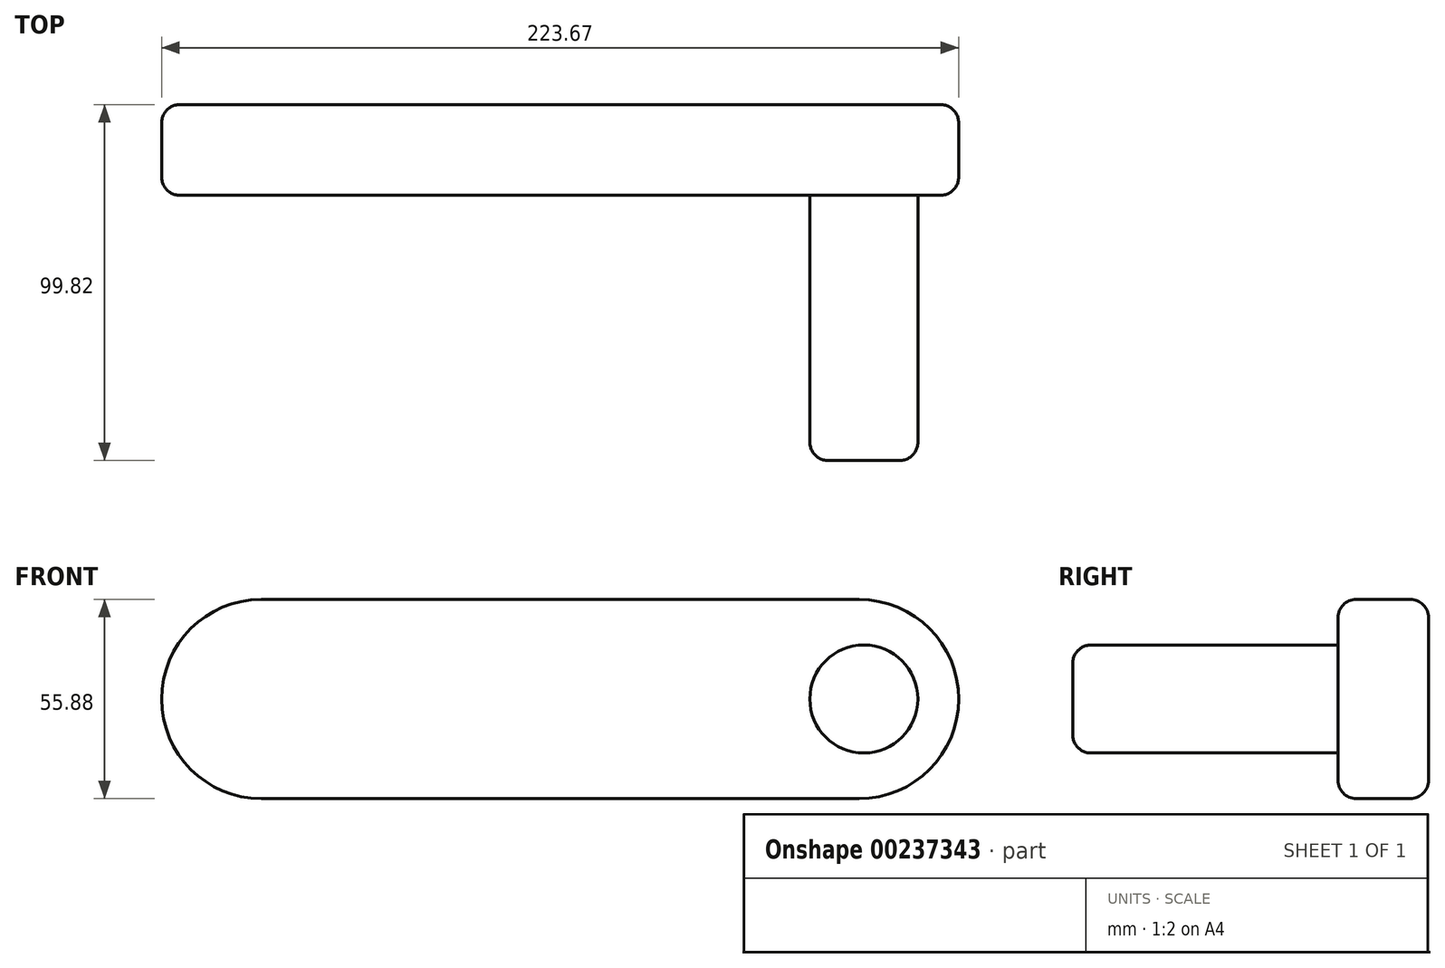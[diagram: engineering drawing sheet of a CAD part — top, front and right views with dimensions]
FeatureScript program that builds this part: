
annotation { "Feature Type Name" : "Feature", "Feature Type Description" : "" }
export const myFeature = defineFeature(function(context is Context, id is Id, definition is map)
    precondition{}
    {
        {
            var Q0;
            Q0=qCreatedBy(makeId("Front.planeOp"),FACE);
            var sketch = newSketch(context, id + "F0", { "sketchPlane" : qUnion([Q0])});
            skCircle(sketch, "E0", {"center": v(-106.88, 0) * mm, "radius": 27.94 * mm});
            skCircle(sketch, "E1", {"center": v(60.9, 0) * mm, "radius": 27.94 * mm});
            skLineSegment(sketch, "E2", {"start": v(-106.88, 27.94) * mm, "end": v(60.9, 27.94) * mm});
            skLineSegment(sketch, "E3", {"start": v(-106.88, -27.94) * mm, "end": v(60.9, -27.94) * mm});
            skSolve(sketch);
        }
        {
            var Q0;
            Q0 = qSketchRegion(id + "F0", true);
            extrude(context, id + "F1", {"entities" : qUnion([Q0]), "depth" : 25.4 * mm});
        }
        {
            var Q0;
            Q0=qCreatedBy(makeId("Front.planeOp"),FACE);
            var sketch = newSketch(context, id + "F2", { "sketchPlane" : qUnion([Q0])});
            skCircle(sketch, "E4", {"center": v(62.24, 0) * mm, "radius": 15.15 * mm});
            skSolve(sketch);
        }
        {
            var Q0;
            Q0 = qSketchRegion(id + "F2", true);
            extrude(context, id + "F3", {"entities" : qUnion([Q0]), "operationType" : NewBodyOperationType.ADD, "depth" : 71.37 * mm});
        }
        {
            var Q0;
            Q0=makeQuery(id+"F3.opExtrude","CAP_FACE",FACE,{"disambiguationData":[OSD([sQuery(id+"F2.wireOp",EDGE,"E4")])],"isStart":false});
            extrude(context, id + "F4", {"entities" : qUnion([Q0]), "operationType" : NewBodyOperationType.ADD, "depth" : 28.45 * mm});
        }
        {
            var Q0;
            Q0=makeQuery(id+"F1.opExtrude","CAP_EDGE",EDGE,{"disambiguationData":[OSD([sQuery(id+"F0.wireOp",EDGE,"E2")])],"isStart":true});
            var Q1;
            Q1=makeQuery(id+"F1.opExtrude","CAP_EDGE",EDGE,{"disambiguationData":[OSD([sQuery(id+"F0.wireOp",EDGE,"E0")])],"isStart":false});
            var Q2;
            Q2=makeQuery(id+"F4.opExtrude","CAP_FACE",FACE,{"disambiguationData":[OSD([sQuery(id+"F2.wireOp",EDGE,"E4")])],"isStart":false});
            fillet(context, id + "F5", {"entities" : qUnion([Q0, Q1, Q2]), "radius" : 5.08 * mm, "tangentPropagation" : true, "allowEdgeOverflow" : false});
        }
    });
